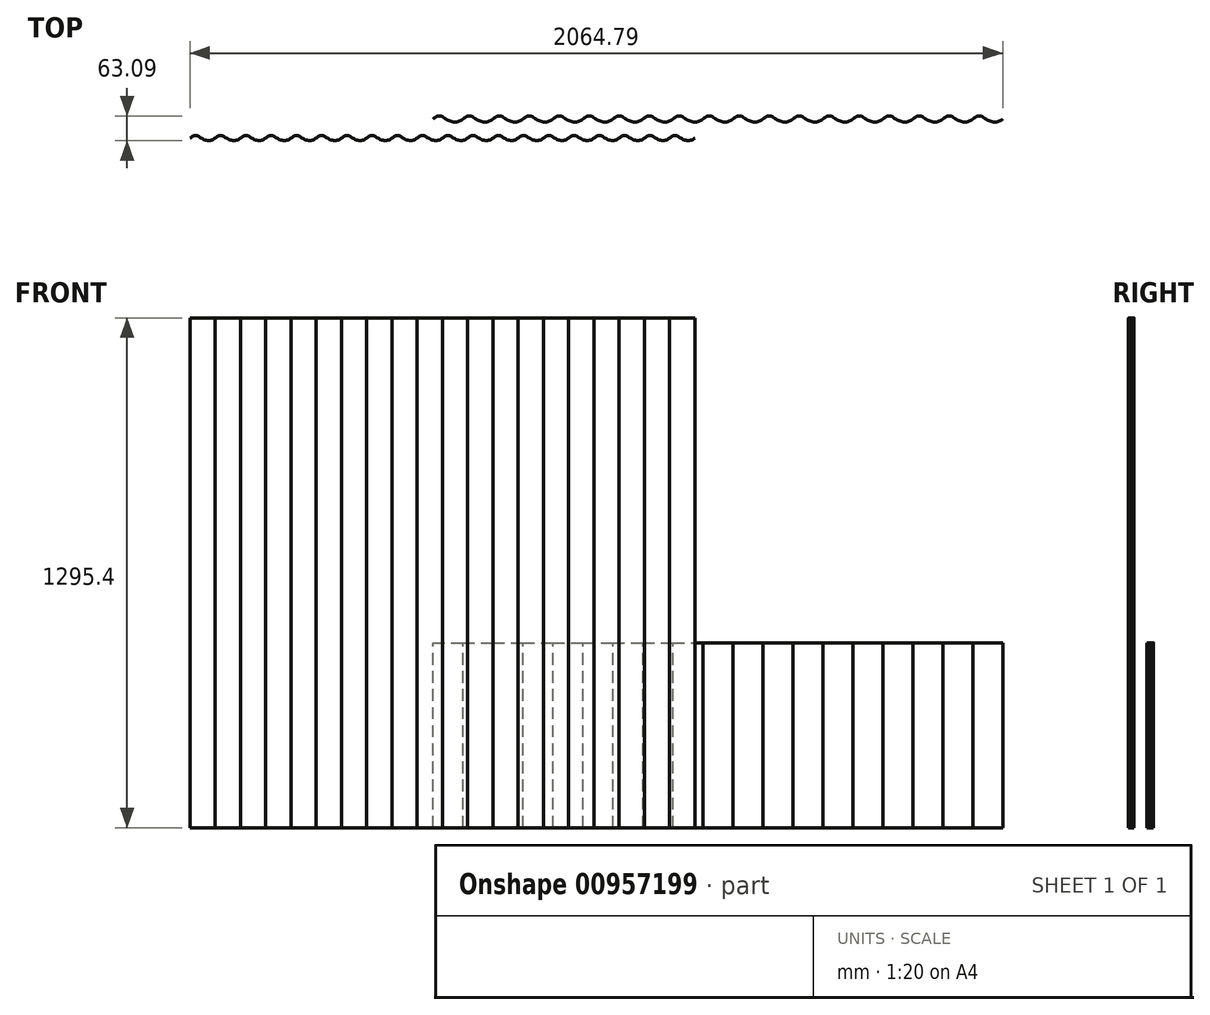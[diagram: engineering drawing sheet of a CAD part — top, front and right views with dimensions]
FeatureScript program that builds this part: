
annotation { "Feature Type Name" : "Feature", "Feature Type Description" : "" }
export const myFeature = defineFeature(function(context is Context, id is Id, definition is map)
    precondition{}
    {
        {
            var Q0;
            Q0=qCreatedBy(makeId("Top.planeOp"),FACE);
            var sketch = newSketch(context, id + "F0", { "sketchPlane" : qUnion([Q0])});
            skFitSpline(sketch, "E0", {"points": [v(-76.2, 0) * mm, v(-59.35, 8.43) * mm, v(-42.5, 0) * mm, v(-18.32, -7.7) * mm, v(0, 0) * mm], "startDerivative": vector(71.9, 53.55) * mm, "endDerivative": vector(70.3, 44.56) * mm});
            skFitSpline(sketch, "E1", {"points": [v(0, 0) * mm, v(16.85, 8.43) * mm, v(33.7, 0) * mm, v(57.88, -7.7) * mm, v(76.2, 0) * mm], "startDerivative": vector(71.9, 53.55) * mm, "endDerivative": vector(70.3, 44.56) * mm});
            skFitSpline(sketch, "E2", {"points": [v(76.2, 0) * mm, v(93.05, 8.43) * mm, v(109.9, 0) * mm, v(134.08, -7.7) * mm, v(152.4, 0) * mm], "startDerivative": vector(71.9, 53.55) * mm, "endDerivative": vector(70.3, 44.56) * mm});
            skFitSpline(sketch, "E3", {"points": [v(152.4, 0) * mm, v(169.25, 8.43) * mm, v(186.1, 0) * mm, v(210.28, -7.7) * mm, v(228.6, 0) * mm], "startDerivative": vector(71.9, 53.55) * mm, "endDerivative": vector(70.3, 44.56) * mm});
            skFitSpline(sketch, "E4", {"points": [v(228.6, 0) * mm, v(245.45, 8.43) * mm, v(262.3, 0) * mm, v(286.48, -7.7) * mm, v(304.8, 0) * mm], "startDerivative": vector(71.9, 53.55) * mm, "endDerivative": vector(70.3, 44.56) * mm});
            skFitSpline(sketch, "E5", {"points": [v(304.8, 0) * mm, v(321.65, 8.43) * mm, v(338.5, 0) * mm, v(362.68, -7.7) * mm, v(381, 0) * mm], "startDerivative": vector(71.9, 53.55) * mm, "endDerivative": vector(70.3, 44.56) * mm});
            skFitSpline(sketch, "E6", {"points": [v(381, 0) * mm, v(397.85, 8.43) * mm, v(414.7, 0) * mm, v(438.88, -7.7) * mm, v(457.2, 0) * mm], "startDerivative": vector(71.9, 53.55) * mm, "endDerivative": vector(70.3, 44.56) * mm});
            skFitSpline(sketch, "E7", {"points": [v(457.2, 0) * mm, v(474.05, 8.43) * mm, v(490.9, 0) * mm, v(515.08, -7.7) * mm, v(533.4, 0) * mm], "startDerivative": vector(71.9, 53.55) * mm, "endDerivative": vector(70.3, 44.56) * mm});
            skFitSpline(sketch, "E8", {"points": [v(533.4, 0) * mm, v(550.25, 8.43) * mm, v(567.1, 0) * mm, v(591.28, -7.7) * mm, v(609.6, 0) * mm], "startDerivative": vector(71.9, 53.55) * mm, "endDerivative": vector(70.3, 44.56) * mm});
            skFitSpline(sketch, "E9", {"points": [v(609.6, 0) * mm, v(626.45, 8.43) * mm, v(643.3, 0) * mm, v(667.48, -7.7) * mm, v(685.8, 0) * mm], "startDerivative": vector(71.9, 53.55) * mm, "endDerivative": vector(70.3, 44.56) * mm});
            skFitSpline(sketch, "E10", {"points": [v(685.8, 0) * mm, v(702.65, 8.43) * mm, v(719.5, 0) * mm, v(743.68, -7.7) * mm, v(762, 0) * mm], "startDerivative": vector(71.9, 53.55) * mm, "endDerivative": vector(70.3, 44.56) * mm});
            skFitSpline(sketch, "E11", {"points": [v(762, 0) * mm, v(778.85, 8.43) * mm, v(795.7, 0) * mm, v(819.88, -7.7) * mm, v(838.2, 0) * mm], "startDerivative": vector(71.9, 53.55) * mm, "endDerivative": vector(70.3, 44.56) * mm});
            skFitSpline(sketch, "E12", {"points": [v(838.2, 0) * mm, v(855.05, 8.43) * mm, v(871.9, 0) * mm, v(896.08, -7.7) * mm, v(914.4, 0) * mm], "startDerivative": vector(71.9, 53.55) * mm, "endDerivative": vector(70.3, 44.56) * mm});
            skFitSpline(sketch, "E13", {"points": [v(914.4, 0) * mm, v(931.25, 8.43) * mm, v(948.1, 0) * mm, v(972.28, -7.7) * mm, v(990.6, 0) * mm], "startDerivative": vector(71.9, 53.55) * mm, "endDerivative": vector(70.3, 44.56) * mm});
            skFitSpline(sketch, "E14", {"points": [v(990.6, 0) * mm, v(1007.45, 8.43) * mm, v(1024.3, 0) * mm, v(1048.48, -7.7) * mm, v(1066.8, 0) * mm], "startDerivative": vector(71.9, 53.55) * mm, "endDerivative": vector(70.3, 44.56) * mm});
            skFitSpline(sketch, "E15", {"points": [v(1066.8, 0) * mm, v(1083.65, 8.43) * mm, v(1100.5, 0) * mm, v(1124.68, -7.7) * mm, v(1143, 0) * mm], "startDerivative": vector(71.9, 53.55) * mm, "endDerivative": vector(70.3, 44.56) * mm});
            skFitSpline(sketch, "E16", {"points": [v(1143, 0) * mm, v(1159.85, 8.43) * mm, v(1176.7, 0) * mm, v(1200.88, -7.7) * mm, v(1219.2, 0) * mm], "startDerivative": vector(71.9, 53.55) * mm, "endDerivative": vector(70.3, 44.56) * mm});
            skFitSpline(sketch, "E17", {"points": [v(1219.2, 0) * mm, v(1236.05, 8.43) * mm, v(1252.9, 0) * mm, v(1277.08, -7.7) * mm, v(1295.4, 0) * mm], "startDerivative": vector(71.9, 53.55) * mm, "endDerivative": vector(70.3, 44.56) * mm});
            skFitSpline(sketch, "E18", {"points": [v(1295.4, 0) * mm, v(1312.25, 8.43) * mm, v(1329.1, 0) * mm, v(1353.28, -7.7) * mm, v(1371.6, 0) * mm], "startDerivative": vector(71.9, 53.55) * mm, "endDerivative": vector(70.3, 44.56) * mm});
            skSolve(sketch);
        }
        {
            var Q0;
            Q0=qCreatedBy(makeId("Top.planeOp"),FACE);
            var sketch = newSketch(context, id + "F1", { "sketchPlane" : qUnion([Q0])});
            skFitSpline(sketch, "E19", {"points": [v(-693.2, -48.15) * mm, v(-679, -41.06) * mm, v(-664.82, -48.15) * mm, v(-644.47, -54.62) * mm, v(-629.06, -48.15) * mm], "startDerivative": vector(60.51, 45.07) * mm, "endDerivative": vector(59.17, 37.5) * mm});
            skFitSpline(sketch, "E20", {"points": [v(-629.06, -48.15) * mm, v(-614.87, -41.06) * mm, v(-600.69, -48.15) * mm, v(-580.34, -54.62) * mm, v(-564.92, -48.15) * mm], "startDerivative": vector(60.51, 45.07) * mm, "endDerivative": vector(59.17, 37.5) * mm});
            skFitSpline(sketch, "E21", {"points": [v(-564.92, -48.15) * mm, v(-550.74, -41.06) * mm, v(-536.55, -48.15) * mm, v(-516.2, -54.62) * mm, v(-500.79, -48.15) * mm], "startDerivative": vector(60.51, 45.07) * mm, "endDerivative": vector(59.17, 37.5) * mm});
            skFitSpline(sketch, "E22", {"points": [v(-500.79, -48.15) * mm, v(-486.6, -41.06) * mm, v(-472.42, -48.15) * mm, v(-452.07, -54.62) * mm, v(-436.65, -48.15) * mm], "startDerivative": vector(60.51, 45.07) * mm, "endDerivative": vector(59.17, 37.5) * mm});
            skFitSpline(sketch, "E23", {"points": [v(-436.65, -48.15) * mm, v(-422.47, -41.06) * mm, v(-408.28, -48.15) * mm, v(-387.93, -54.62) * mm, v(-372.52, -48.15) * mm], "startDerivative": vector(60.51, 45.07) * mm, "endDerivative": vector(59.17, 37.5) * mm});
            skFitSpline(sketch, "E24", {"points": [v(-372.52, -48.15) * mm, v(-358.33, -41.06) * mm, v(-344.15, -48.15) * mm, v(-323.8, -54.62) * mm, v(-308.38, -48.15) * mm], "startDerivative": vector(60.51, 45.07) * mm, "endDerivative": vector(59.17, 37.5) * mm});
            skFitSpline(sketch, "E25", {"points": [v(-308.38, -48.15) * mm, v(-294.2, -41.06) * mm, v(-280.01, -48.15) * mm, v(-259.66, -54.62) * mm, v(-244.25, -48.15) * mm], "startDerivative": vector(60.51, 45.07) * mm, "endDerivative": vector(59.17, 37.5) * mm});
            skFitSpline(sketch, "E26", {"points": [v(-244.25, -48.15) * mm, v(-230.06, -41.06) * mm, v(-215.88, -48.15) * mm, v(-195.53, -54.62) * mm, v(-180.11, -48.15) * mm], "startDerivative": vector(60.51, 45.07) * mm, "endDerivative": vector(59.17, 37.5) * mm});
            skFitSpline(sketch, "E27", {"points": [v(-180.11, -48.15) * mm, v(-165.93, -41.06) * mm, v(-151.74, -48.15) * mm, v(-131.4, -54.62) * mm, v(-115.98, -48.15) * mm], "startDerivative": vector(60.51, 45.07) * mm, "endDerivative": vector(59.17, 37.5) * mm});
            skFitSpline(sketch, "E28", {"points": [v(-115.98, -48.15) * mm, v(-101.8, -41.06) * mm, v(-87.6, -48.15) * mm, v(-67.26, -54.62) * mm, v(-51.84, -48.15) * mm], "startDerivative": vector(60.51, 45.07) * mm, "endDerivative": vector(59.17, 37.5) * mm});
            skFitSpline(sketch, "E29", {"points": [v(-51.84, -48.15) * mm, v(-37.66, -41.06) * mm, v(-23.47, -48.15) * mm, v(-3.12, -54.62) * mm, v(12.3, -48.15) * mm], "startDerivative": vector(60.51, 45.07) * mm, "endDerivative": vector(59.17, 37.5) * mm});
            skFitSpline(sketch, "E30", {"points": [v(12.3, -48.15) * mm, v(26.48, -41.06) * mm, v(40.66, -48.15) * mm, v(61.01, -54.62) * mm, v(76.43, -48.15) * mm], "startDerivative": vector(60.51, 45.07) * mm, "endDerivative": vector(59.17, 37.5) * mm});
            skFitSpline(sketch, "E31", {"points": [v(76.43, -48.15) * mm, v(90.61, -41.06) * mm, v(104.8, -48.15) * mm, v(125.15, -54.62) * mm, v(140.56, -48.15) * mm], "startDerivative": vector(60.51, 45.07) * mm, "endDerivative": vector(59.17, 37.5) * mm});
            skFitSpline(sketch, "E32", {"points": [v(140.56, -48.15) * mm, v(154.75, -41.06) * mm, v(168.93, -48.15) * mm, v(189.28, -54.62) * mm, v(204.7, -48.15) * mm], "startDerivative": vector(60.51, 45.07) * mm, "endDerivative": vector(59.17, 37.5) * mm});
            skFitSpline(sketch, "E33", {"points": [v(204.7, -48.15) * mm, v(218.88, -41.06) * mm, v(233.07, -48.15) * mm, v(253.42, -54.62) * mm, v(268.83, -48.15) * mm], "startDerivative": vector(60.51, 45.07) * mm, "endDerivative": vector(59.17, 37.5) * mm});
            skFitSpline(sketch, "E34", {"points": [v(268.83, -48.15) * mm, v(283.02, -41.06) * mm, v(297.2, -48.15) * mm, v(317.55, -54.62) * mm, v(332.97, -48.15) * mm], "startDerivative": vector(60.51, 45.07) * mm, "endDerivative": vector(59.17, 37.5) * mm});
            skFitSpline(sketch, "E35", {"points": [v(332.97, -48.15) * mm, v(347.15, -41.06) * mm, v(361.34, -48.15) * mm, v(381.69, -54.62) * mm, v(397.1, -48.15) * mm], "startDerivative": vector(60.51, 45.07) * mm, "endDerivative": vector(59.17, 37.5) * mm});
            skFitSpline(sketch, "E36", {"points": [v(397.1, -48.15) * mm, v(411.29, -41.06) * mm, v(425.47, -48.15) * mm, v(445.82, -54.62) * mm, v(461.24, -48.15) * mm], "startDerivative": vector(60.51, 45.07) * mm, "endDerivative": vector(59.17, 37.5) * mm});
            skFitSpline(sketch, "E37", {"points": [v(461.24, -48.15) * mm, v(475.42, -41.06) * mm, v(489.6, -48.15) * mm, v(509.96, -54.62) * mm, v(525.37, -48.15) * mm], "startDerivative": vector(60.51, 45.07) * mm, "endDerivative": vector(59.17, 37.5) * mm});
            skFitSpline(sketch, "E38", {"points": [v(525.37, -48.15) * mm, v(539.56, -41.06) * mm, v(553.74, -48.15) * mm, v(574.1, -54.62) * mm, v(589.5, -48.15) * mm], "startDerivative": vector(60.51, 45.07) * mm, "endDerivative": vector(59.17, 37.5) * mm});
            skSolve(sketch);
        }
        {
            var Q0;
            Q0=qSketchRegion(id+"F0",true);
            var Q1;
            Q1=qConstructionFilter(qBodyType(qCreatedBy(id+"F0",EDGE),BodyType.WIRE),ConstructionObject.NO);
            extrude(context, id + "F2", {"entities" : qUnion([Q0]), "bodyType" : ToolBodyType.SURFACE, "operationType" : NewBodyOperationType.ADD, "surfaceEntities" : qUnion([Q1]), "depth" : 469.9 * mm, "offsetDistance" : 25.4 * mm});
        }
        {
            var Q0;
            Q0=qSketchRegion(id+"F1",true);
            var Q1;
            Q1=qConstructionFilter(qBodyType(qCreatedBy(id+"F1",EDGE),BodyType.WIRE),ConstructionObject.NO);
            extrude(context, id + "F3", {"entities" : qUnion([Q0]), "bodyType" : ToolBodyType.SURFACE, "surfaceEntities" : qUnion([Q1]), "depth" : 1295.4 * mm, "offsetDistance" : 25.4 * mm});
        }
    });
